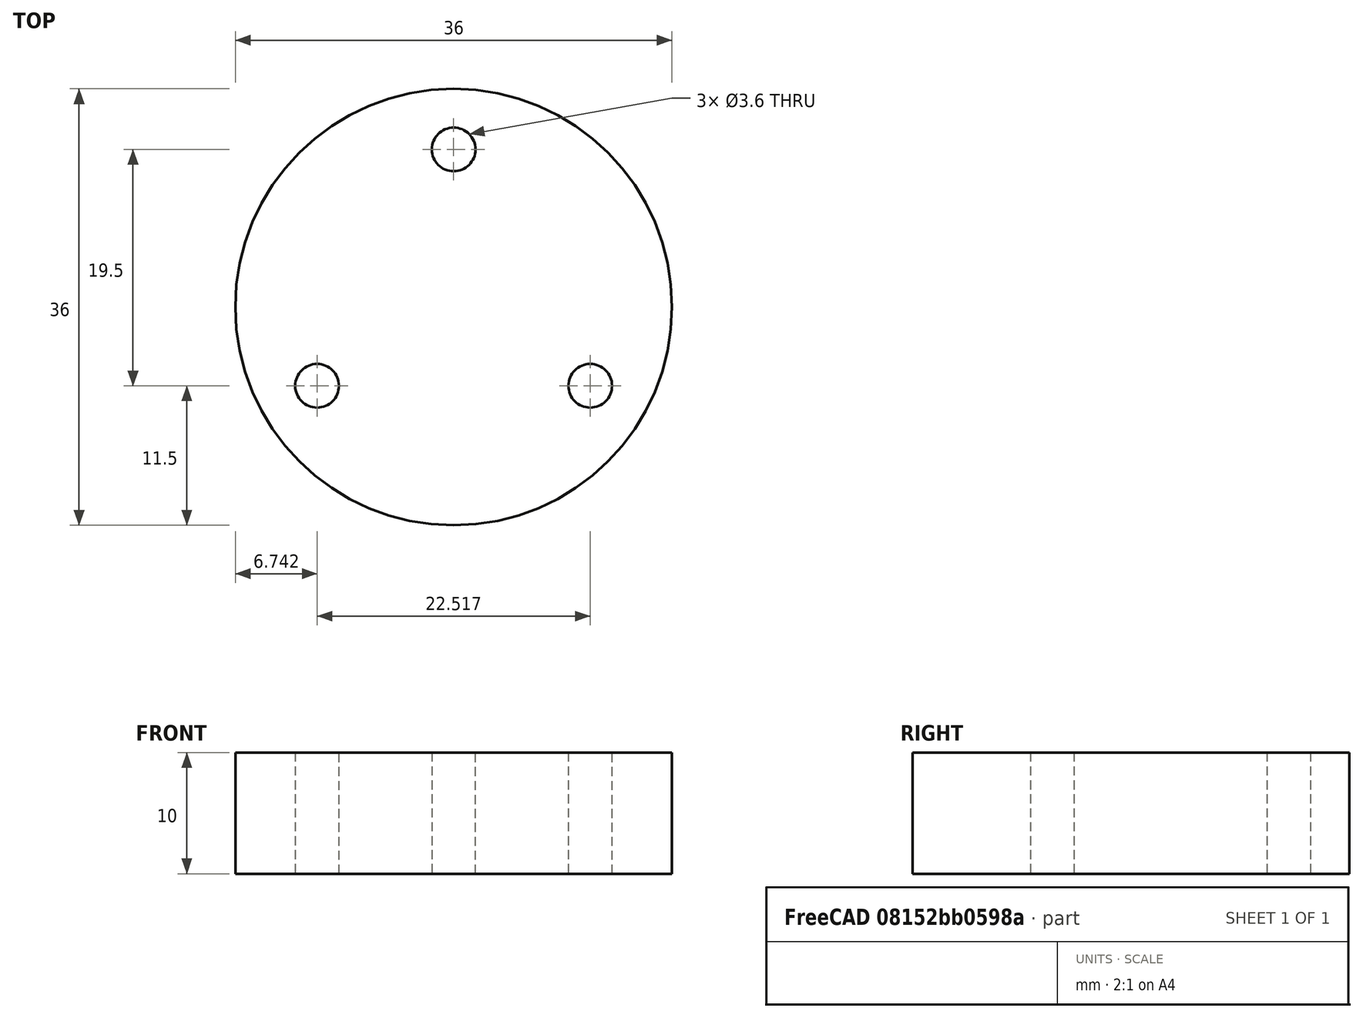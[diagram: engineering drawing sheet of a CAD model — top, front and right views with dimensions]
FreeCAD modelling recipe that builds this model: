
FCSTD DOCUMENT  (FreeCAD 0.15R4671 (Git))
Label: AdaptorSpacer
License: All rights reserved
LicenseURL: http://en.wikipedia.org/wiki/All_rights_reserved
objects: Sketcher::SketchObject×1, PartDesign::Pad×1
note: 3 computed .brp shape members not serialized (recipe doc carries the construction recipe); baked Part::Feature solids carry a one-line shape summary decoded from their .brp

FEATURE [Sketcher::SketchObject] Sketch
  sketch-geometry (8):
    g0: Circle CenterX=-11.2583 CenterY=-6.5 CenterZ=0 NormalX=0 NormalY=0 NormalZ=1 Radius=1.8
    g1: Circle CenterX=11.2583 CenterY=-6.5 CenterZ=0 NormalX=0 NormalY=0 NormalZ=1 Radius=1.8
    g2: Circle CenterX=0 CenterY=13 CenterZ=0 NormalX=0 NormalY=0 NormalZ=1 Radius=1.8
    g3: LineSegment [constr] StartX=0 StartY=0 StartZ=0 EndX=0 EndY=18 EndZ=0
    g4: LineSegment [constr] StartX=0 StartY=0 StartZ=0 EndX=-15.5885 EndY=-9 EndZ=0
    g5: LineSegment [constr] StartX=0 StartY=0 StartZ=0 EndX=15.5885 EndY=-9 EndZ=0
    g6: Circle [constr] CenterX=0 CenterY=0 CenterZ=0 NormalX=0 NormalY=0 NormalZ=1 Radius=13
    g7: Circle CenterX=0 CenterY=0 CenterZ=0 NormalX=0 NormalY=0 NormalZ=1 Radius=18
  constraints (22):
    c: Coincident(g3,g-1)
    c: Vertical(g3)
    c: Coincident(g4,g-1)
    c: Coincident(g5,g-1)
    c: Angle(g5,g3) = 2.0944
    c: Angle(g4,g5) = 2.0944
    c: PointOnObject(g0,g4)
    c: PointOnObject(g1,g5)
    c: PointOnObject(g2,g3)
    c: Coincident(g6,g-1)
    c: PointOnObject(g1,g6)
    c: PointOnObject(g0,g6)
    c: PointOnObject(g2,g6)
    c: Radius(g1) = 1.8
    c: Equal(g1,g0)
    c: Equal(g1,g2)
    c: Radius(g6) = 13
    c: Coincident(g7,g-1)
    c: Radius(g7) = 18
    c: PointOnObject(g4,g7)
    c: PointOnObject(g3,g7)
    c: PointOnObject(g5,g7)
FEATURE [PartDesign::Pad] Pad
  Length = 10
  Length2 = 100
  Sketch = -> Sketch
  Type = 0
